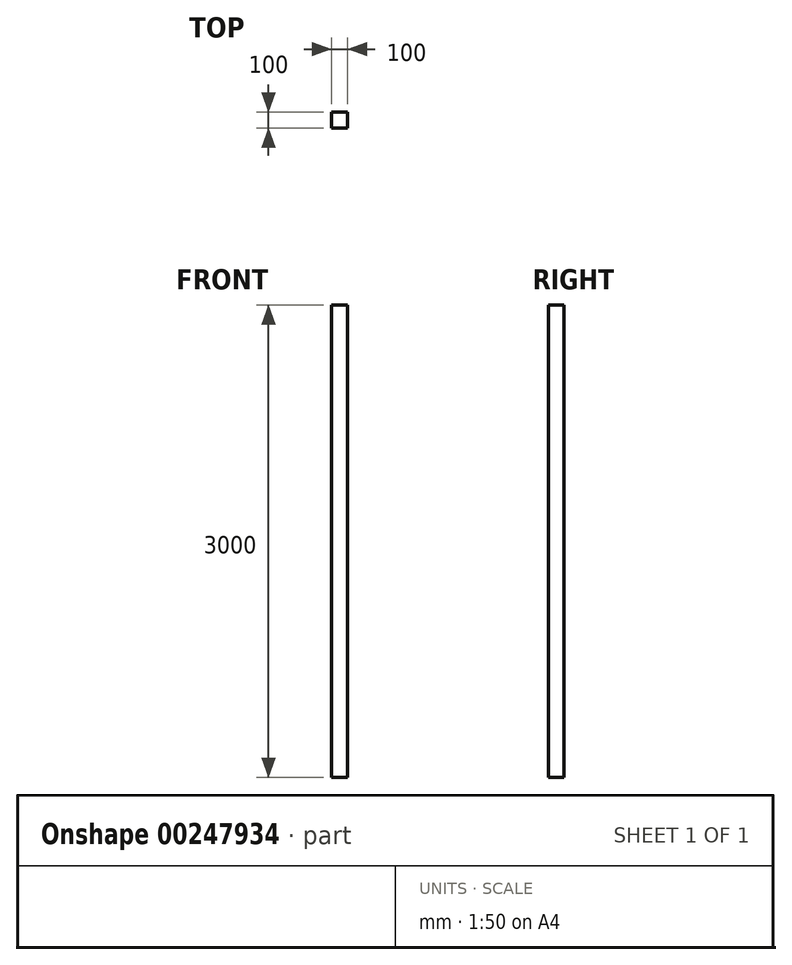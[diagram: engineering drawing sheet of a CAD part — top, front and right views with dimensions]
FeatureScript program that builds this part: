
annotation { "Feature Type Name" : "Feature", "Feature Type Description" : "" }
export const myFeature = defineFeature(function(context is Context, id is Id, definition is map)
    precondition{}
    {
        {
            var Q0;
            Q0=qCreatedBy(makeId("Front.planeOp"),FACE);
            var sketch = newSketch(context, id + "F0", { "sketchPlane" : qUnion([Q0])});
            skLineSegment(sketch, "E0.bottom", {"start": v(50, 0) * mm, "end": v(-50, 0) * mm});
            skLineSegment(sketch, "E0.top", {"start": v(50, 3000) * mm, "end": v(-50, 3000) * mm});
            skLineSegment(sketch, "E0.left", {"start": v(50, 0) * mm, "end": v(50, 3000) * mm});
            skLineSegment(sketch, "E0.right", {"start": v(-50, 0) * mm, "end": v(-50, 3000) * mm});
            skPoint(sketch, "E0.middle", {"position": v(0, 1500) * mm});
            skSolve(sketch);
        }
        {
            var Q0;
            Q0=makeQuery(id+"F0.imprint","IMPRINT",FACE,{"disambiguationData":[TD([[makeQuery(id+"F0.imprint","IMPRINT",EDGE,{"derivedFrom":sQuery(id+"F0.wireOp",EDGE,"E0.bottom")}),-1.0]])]});
            extrude(context, id + "F1", {"entities" : qUnion([Q0]), "endBound" : BoundingType.SYMMETRIC, "depth" : 100 * mm});
        }
    });
